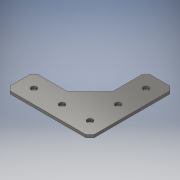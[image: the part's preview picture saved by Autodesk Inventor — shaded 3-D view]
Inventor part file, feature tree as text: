
AUTODESK INVENTOR PART (.ipt)
format: ipt  version: 2017 (Build 210142000, 142)  size: 112,640 bytes
history: native  units: in
note: dims shown in document units (in); Inventor stores cm internally (conversion verified against a paired STEP export)
features: extrude x1, sketch x1
ambient origin geometry x8: Origin, YZ Plane, XZ Plane, XY Plane, X Axis, Y Axis, Z Axis, Center Point
bodies: Solid1 (feature_tree)
feature tree (2):
  extrude  "Extrusion1"  [1 undecoded]
  sketch  "Sketch1"  dims[d24=0.1in d25=0.0in]
note: 1 required parameter value undecoded (feature->parameter linkage not recoverable at this tier; creation-order binding heuristic only, values carry confidence <= 0.55)
